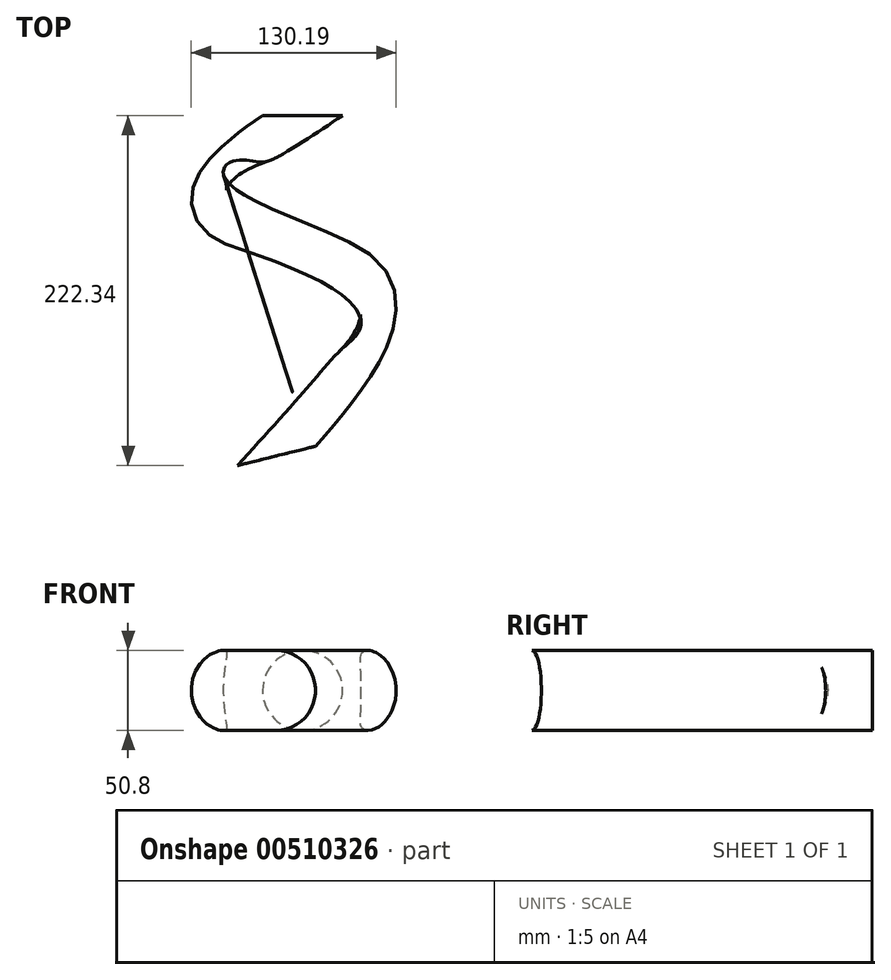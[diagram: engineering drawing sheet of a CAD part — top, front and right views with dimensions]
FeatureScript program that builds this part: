
annotation { "Feature Type Name" : "Feature", "Feature Type Description" : "" }
export const myFeature = defineFeature(function(context is Context, id is Id, definition is map)
    precondition{}
    {
        {
            var Q0;
            Q0=qCreatedBy(makeId("Front.planeOp"),FACE);
            var sketch = newSketch(context, id + "F0", { "sketchPlane" : qUnion([Q0])});
            skCircle(sketch, "E0", {"center": v(0, 0) * mm, "radius": 25.4 * mm});
            skSolve(sketch);
        }
        {
            var Q0;
            Q0=qCreatedBy(makeId("Top.planeOp"),FACE);
            var sketch = newSketch(context, id + "F1", { "sketchPlane" : qUnion([Q0])});
            skFitSpline(sketch, "E1", {"points": [v(0, 0) * mm, v(-49.06, -55) * mm, v(37.18, -110.25) * mm, v(-16.52, -216.24) * mm], "startDerivative": vector(-296.16, -204) * mm, "endDerivative": vector(-287.9, -324.97) * mm});
            skSolve(sketch);
        }
        {
            var Q0;
            Q0=makeQuery(id+"F0.imprint","IMPRINT",FACE,{"disambiguationData":[TD([[makeQuery(id+"F0.imprint","IMPRINT",EDGE,{"derivedFrom":sQuery(id+"F0.wireOp",EDGE,"E0")}),1.0]])]});
            var Q1;
            Q1=sQuery(id+"F1.wireOp",EDGE,"E1");
            sweep(context, id + "F2", {"profiles" : qUnion([Q0]), "path" : qUnion([Q1])});
        }
    });
